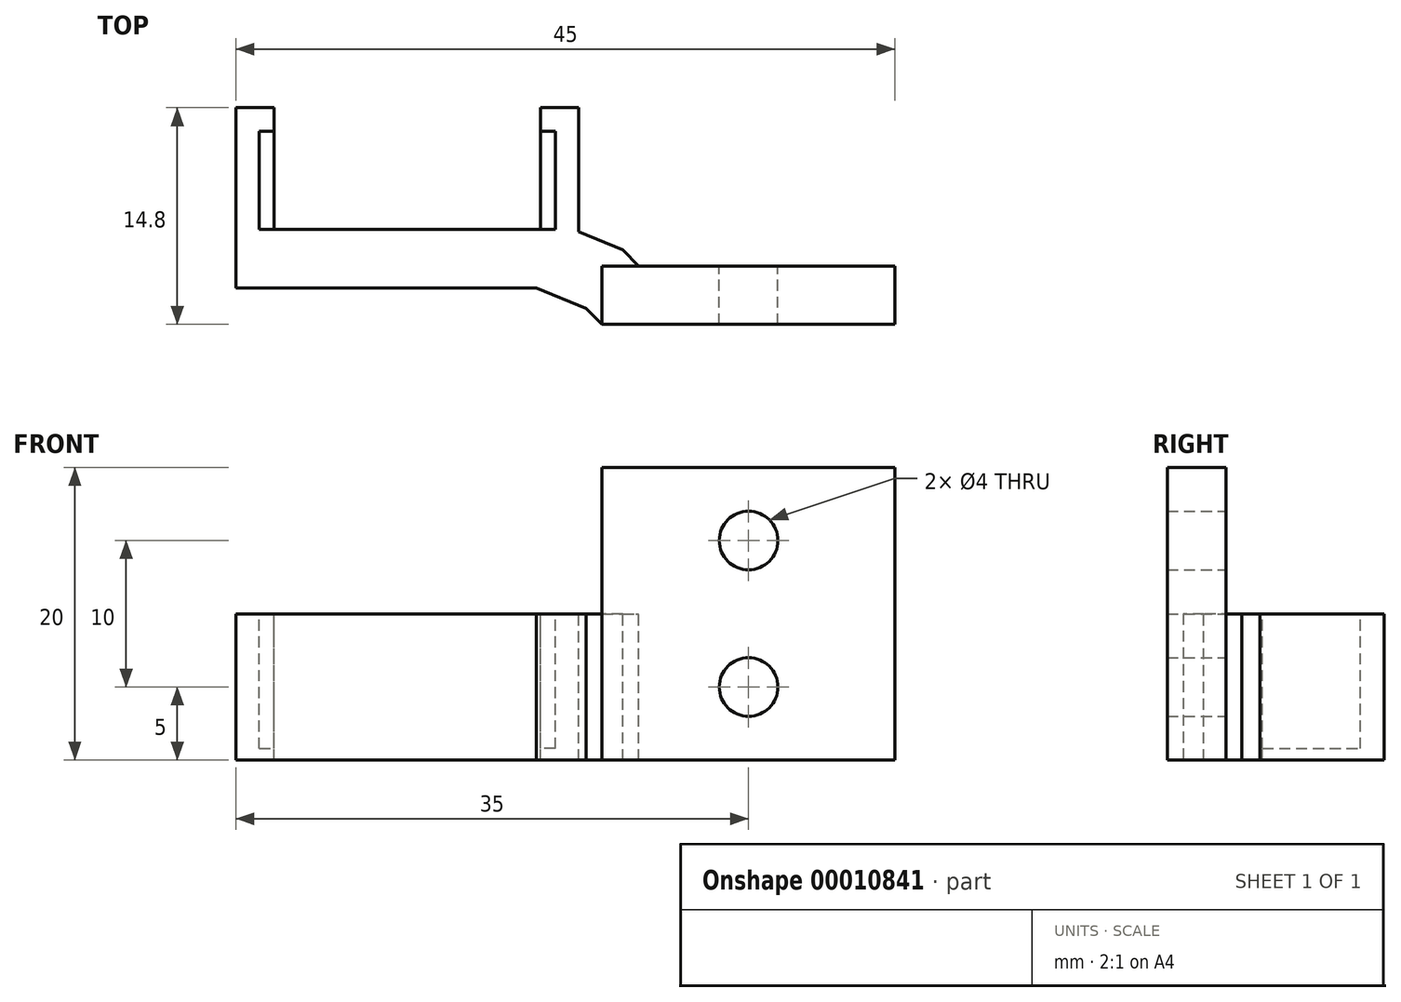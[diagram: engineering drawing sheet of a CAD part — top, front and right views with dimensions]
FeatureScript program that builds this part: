
annotation { "Feature Type Name" : "Feature", "Feature Type Description" : "" }
export const myFeature = defineFeature(function(context is Context, id is Id, definition is map)
    precondition{}
    {
        {
            var Q0;
            Q0=qCreatedBy(makeId("Top.planeOp"),FACE);
            var sketch = newSketch(context, id + "F0", { "sketchPlane" : qUnion([Q0])});
            skLineSegment(sketch, "E0", {"start": v(-10.1, -3.35) * mm, "end": v(-9.1, -3.35) * mm});
            skLineSegment(sketch, "E1", {"start": v(-9.1, -3.35) * mm, "end": v(-9.1, -4.95) * mm});
            skLineSegment(sketch, "E2", {"start": v(-9.1, -4.95) * mm, "end": v(-11.7, -4.95) * mm});
            skLineSegment(sketch, "E3", {"start": v(-11.7, -4.95) * mm, "end": v(-11.7, 7.35) * mm});
            skLineSegment(sketch, "E4", {"start": v(-11.7, 7.35) * mm, "end": v(11.7, 7.35) * mm});
            skLineSegment(sketch, "E5", {"start": v(11.7, 7.35) * mm, "end": v(11.7, -4.95) * mm});
            skLineSegment(sketch, "E6", {"start": v(11.7, -4.95) * mm, "end": v(9.1, -4.95) * mm});
            skLineSegment(sketch, "E7", {"start": v(9.1, -4.95) * mm, "end": v(9.1, -3.35) * mm});
            skLineSegment(sketch, "E8", {"start": v(9.1, -3.35) * mm, "end": v(10.1, -3.35) * mm});
            skLineSegment(sketch, "E9", {"start": v(10.1, -3.35) * mm, "end": v(10.1, 3.35) * mm});
            skLineSegment(sketch, "E10", {"start": v(10.1, 3.35) * mm, "end": v(-10.1, 3.35) * mm});
            skLineSegment(sketch, "E11", {"start": v(-10.1, 3.35) * mm, "end": v(-10.1, -3.35) * mm});
            skLineSegment(sketch, "E12", {"start": v(11.7, 7.35) * mm, "end": v(33.3, 7.35) * mm});
            skLineSegment(sketch, "E13", {"start": v(33.3, 7.35) * mm, "end": v(33.3, 3.35) * mm});
            skLineSegment(sketch, "E14", {"start": v(33.3, 3.35) * mm, "end": v(11.7, 3.35) * mm});
            skLineSegment(sketch, "E15", {"start": v(13.3, 7.35) * mm, "end": v(13.3, 3.35) * mm});
            skLineSegment(sketch, "E16", {"start": v(13.3, 7.35) * mm, "end": v(13.3, 9.85) * mm});
            skLineSegment(sketch, "E17", {"start": v(13.3, 9.85) * mm, "end": v(33.3, 9.85) * mm});
            skLineSegment(sketch, "E18", {"start": v(33.3, 9.85) * mm, "end": v(33.3, 7.35) * mm});
            skLineSegment(sketch, "E19", {"start": v(13.3, 5.85) * mm, "end": v(33.3, 5.85) * mm});
            skLineSegment(sketch, "E20", {"start": v(13.3, 9.85) * mm, "end": v(10.8, 7.35) * mm});
            skLineSegment(sketch, "E21", {"start": v(13.3, 3.35) * mm, "end": v(15.8, 5.85) * mm});
            skSolve(sketch);
        }
        {
            var Q0;
            Q0=makeQuery(id+"F0.imprint","IMPRINT",FACE,{"disambiguationData":[TD([[makeQuery(id+"F0.imprint","IMPRINT",EDGE,{"derivedFrom":sQuery(id+"F0.wireOp",EDGE,"E0")}),-1.0]])]});
            var Q1;
            {var subQ0=sQuery(id+"F0.wireOp",EDGE,"E15");Q1=makeQuery(id+"F0.imprint","IMPRINT",FACE,{"disambiguationData":[TD([[makeQuery(id+"F0.imprint","IMPRINT",EDGE,{"derivedFrom":subQ0}),-1.0]])]});}
            var Q2;
            {var subQ1=sQuery(id+"F0.wireOp",EDGE,"E12");Q2=makeQuery(id+"F0.imprint","IMPRINT",FACE,{"disambiguationData":[TD([[makeQuery(id+"F0.imprint","IMPRINT",EDGE,{"derivedFrom":subQ1}),1.0]])]});}
            var Q3;
            {var subQ2=sQuery(id+"F0.wireOp",EDGE,"E15");Q3=makeQuery(id+"F0.imprint","IMPRINT",FACE,{"disambiguationData":[TD([[makeQuery(id+"F0.imprint","IMPRINT",EDGE,{"derivedFrom":subQ2}),1.0]])]});}
            extrude(context, id + "F1", {"entities" : qUnion([Q0, Q1, Q2, Q3]), "depth" : 9.2 * mm});
        }
        {
            var Q0;
            {var subQ0=sQuery(id+"F0.wireOp",EDGE,"E19");Q0=makeQuery(id+"F0.imprint","IMPRINT",FACE,{"disambiguationData":[TD([[makeQuery(id+"F0.imprint","IMPRINT",EDGE,{"derivedFrom":subQ0}),1.0]])]});}
            var Q1;
            {var subQ1=sQuery(id+"F0.wireOp",EDGE,"E16");Q1=makeQuery(id+"F0.imprint","IMPRINT",FACE,{"disambiguationData":[TD([[makeQuery(id+"F0.imprint","IMPRINT",EDGE,{"derivedFrom":subQ1}),-1.0]])]});}
            extrude(context, id + "F2", {"entities" : qUnion([Q0, Q1]), "operationType" : NewBodyOperationType.ADD, "depth" : 20 * mm, "symmetric" : true});
        }
        {
            var Q0;
            Q0=makeQuery(id+"F2.opExtrude","SWEPT_FACE",FACE,{"disambiguationData":[OSD([sQuery(id+"F0.wireOp",EDGE,"E19")])]});
            var sketch = newSketch(context, id + "F3", { "sketchPlane" : qUnion([Q0])});
            skCircle(sketch, "E22", {"center": v(23.3, 5) * mm, "radius": 2 * mm});
            skCircle(sketch, "E23", {"center": v(23.3, -5) * mm, "radius": 2 * mm});
            skSolve(sketch);
        }
        {
            var Q0;
            Q0=makeQuery(id+"F3.imprint","IMPRINT",FACE,{"disambiguationData":[TD([[makeQuery(id+"F3.imprint","IMPRINT",EDGE,{"derivedFrom":sQuery(id+"F3.wireOp",EDGE,"E22")}),1.0]])]});
            var Q1;
            Q1=makeQuery(id+"F3.imprint","IMPRINT",FACE,{"disambiguationData":[TD([[makeQuery(id+"F3.imprint","IMPRINT",EDGE,{"derivedFrom":sQuery(id+"F3.wireOp",EDGE,"E23")}),1.0]])]});
            extrude(context, id + "F4", {"entities" : qUnion([Q0, Q1]), "operationType" : NewBodyOperationType.REMOVE, "oppositeDirection" : true, "depth" : 25 * mm});
        }
        {
            var Q0;
            Q0=makeQuery(id+"F1.opExtrude","CAP_FACE",FACE,{"disambiguationData":[OSD([sQuery(id+"F0.wireOp",EDGE,"E0"),sQuery(id+"F0.wireOp",EDGE,"E1"),sQuery(id+"F0.wireOp",EDGE,"E2"),sQuery(id+"F0.wireOp",EDGE,"E3"),sQuery(id+"F0.wireOp",EDGE,"E4"),sQuery(id+"F0.wireOp",EDGE,"E5"),sQuery(id+"F0.wireOp",EDGE,"E6"),sQuery(id+"F0.wireOp",EDGE,"E7"),sQuery(id+"F0.wireOp",EDGE,"E8"),sQuery(id+"F0.wireOp",EDGE,"E9"),sQuery(id+"F0.wireOp",EDGE,"E10"),sQuery(id+"F0.wireOp",EDGE,"E11"),sQuery(id+"F0.wireOp",EDGE,"E12"),sQuery(id+"F0.wireOp",EDGE,"E14"),sQuery(id+"F0.wireOp",EDGE,"E15")])],"isStart":false});
            var sketch = newSketch(context, id + "F5", { "sketchPlane" : qUnion([Q0])});
            skLineSegment(sketch, "E24", {"start": v(-9.1, -3.35) * mm, "end": v(-9.1, 3.35) * mm});
            skLineSegment(sketch, "E25", {"start": v(9.1, -3.35) * mm, "end": v(9.1, 3.35) * mm});
            skSolve(sketch);
        }
        {
            var Q0;
            Q0=makeQuery(id+"F5.imprint","IMPRINT",FACE,{"disambiguationData":[TD([[makeQuery(id+"F5.imprint","IMPRINT",EDGE,{"derivedFrom":makeQuery(id+"F1.opExtrude","CAP_EDGE",EDGE,{"disambiguationData":[OSD([sQuery(id+"F0.wireOp",EDGE,"E0")])],"isStart":false})}),-1.0]])]});
            var Q1;
            {var subQ1=sQuery(id+"F5.wireOp",EDGE,"E24");Q1=makeQuery(id+"F5.imprint","IMPRINT",FACE,{"disambiguationData":[TD([[makeQuery(id+"F5.imprint","IMPRINT",EDGE,{"derivedFrom":subQ1}),1.0]])]});}
            var Q2;
            {var subQ1=sQuery(id+"F5.wireOp",EDGE,"E25");Q2=makeQuery(id+"F5.imprint","IMPRINT",FACE,{"disambiguationData":[TD([[makeQuery(id+"F5.imprint","IMPRINT",EDGE,{"derivedFrom":subQ1}),-1.0]])]});}
            var Q3;
            Q3=makeQuery(id+"F2.opExtrude","CAP_FACE",FACE,{"disambiguationData":[OSD([sQuery(id+"F0.wireOp",EDGE,"E13"),sQuery(id+"F0.wireOp",EDGE,"E15"),sQuery(id+"F0.wireOp",EDGE,"E16"),sQuery(id+"F0.wireOp",EDGE,"E17"),sQuery(id+"F0.wireOp",EDGE,"E18"),sQuery(id+"F0.wireOp",EDGE,"E19")])],"isStart":false});
            extrude(context, id + "F6", {"entities" : qUnion([Q0, Q1, Q2]), "operationType" : NewBodyOperationType.ADD, "endBound" : BoundingType.UP_TO_SURFACE, "endBoundEntityFace" : qUnion([Q3]), "depth" : 1 * mm});
        }
        {
            var Q0;
            {var subQ0=sQuery(id+"F0.wireOp",EDGE,"E4");var subQ1=sQuery(id+"F0.wireOp",EDGE,"E20");Q0=makeQuery(id+"F6.boolean.opBoolean","MERGE",EDGE,{"derivedFrom":[makeQuery(id+"F1.opExtrude","SWEPT_EDGE",EDGE,{"disambiguationData":[OSD([subQ0,subQ1])]}),makeQuery(id+"F6.opExtrude","SWEPT_EDGE",EDGE,{"disambiguationData":[OSD([subQ0,subQ1])]})]});}
            var Q1;
            {var subQ0=sQuery(id+"F0.wireOp",EDGE,"E14");var subQ1=sQuery(id+"F0.wireOp",EDGE,"E21");Q1=makeQuery(id+"F6.boolean.opBoolean","MERGE",EDGE,{"derivedFrom":[makeQuery(id+"F1.opExtrude","SWEPT_EDGE",EDGE,{"disambiguationData":[OSD([subQ0,sQuery(id+"F0.wireOp",EDGE,"E15"),subQ1])]}),makeQuery(id+"F6.opExtrude","SWEPT_EDGE",EDGE,{"disambiguationData":[OSD([subQ0,subQ1])]})]});}
            chamfer(context, id + "F7", {"entities" : qUnion([Q0, Q1]), "width" : 2 * mm, "tangentPropagation" : true});
        }
        {
            var Q0;
            Q0=makeQuery(id+"F1.opExtrude","SWEPT_BODY",BODY,{"disambiguationData":[OSD([sQuery(id+"F0.wireOp",EDGE,"E0"),sQuery(id+"F0.wireOp",EDGE,"E1"),sQuery(id+"F0.wireOp",EDGE,"E2"),sQuery(id+"F0.wireOp",EDGE,"E3"),sQuery(id+"F0.wireOp",EDGE,"E4"),sQuery(id+"F0.wireOp",EDGE,"E5"),sQuery(id+"F0.wireOp",EDGE,"E6"),sQuery(id+"F0.wireOp",EDGE,"E7"),sQuery(id+"F0.wireOp",EDGE,"E8"),sQuery(id+"F0.wireOp",EDGE,"E9"),sQuery(id+"F0.wireOp",EDGE,"E10"),sQuery(id+"F0.wireOp",EDGE,"E11"),sQuery(id+"F0.wireOp",EDGE,"E12"),sQuery(id+"F0.wireOp",EDGE,"E14"),sQuery(id+"F0.wireOp",EDGE,"E15"),sQuery(id+"F0.wireOp",EDGE,"E17"),sQuery(id+"F0.wireOp",EDGE,"E18"),sQuery(id+"F0.wireOp",EDGE,"E19"),sQuery(id+"F0.wireOp",EDGE,"E20"),sQuery(id+"F0.wireOp",EDGE,"E21")])]});
            var Q1;
            Q1=makeQuery(id+"F2.opExtrude","CAP_EDGE",EDGE,{"disambiguationData":[OSD([sQuery(id+"F0.wireOp",EDGE,"E19")])],"isStart":false});
            transform(context, id + "F8", {"entities" : qUnion([Q0]), "transformType" : TransformType.ROTATION, "transformAxis" : qUnion([Q1]), "angle" : 180 * degree, "makeCopy" : false});
        }
    });
